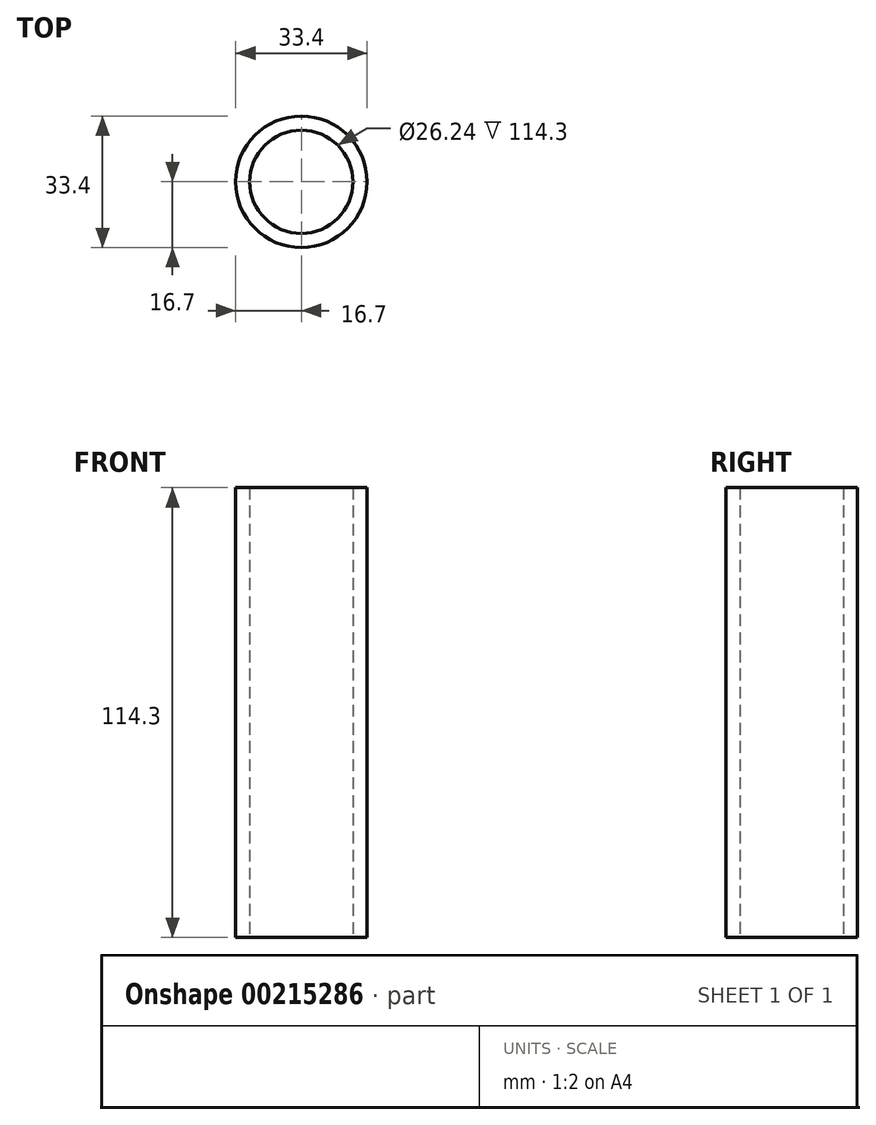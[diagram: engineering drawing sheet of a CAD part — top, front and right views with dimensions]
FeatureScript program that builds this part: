
annotation { "Feature Type Name" : "Feature", "Feature Type Description" : "" }
export const myFeature = defineFeature(function(context is Context, id is Id, definition is map)
    precondition{}
    {
        {
            var Q0;
            Q0=qCreatedBy(makeId("Top.planeOp"),FACE);
            var sketch = newSketch(context, id + "F0", { "sketchPlane" : qUnion([Q0])});
            skCircle(sketch, "E0", {"center": v(0, 0) * mm, "radius": 16.7 * mm});
            skCircle(sketch, "E1", {"center": v(0, 0) * mm, "radius": 13.12 * mm});
            skSolve(sketch);
        }
        {
            var Q0;
            Q0=makeQuery(id+"F0.imprint","IMPRINT",FACE,{"disambiguationData":[TD([[makeQuery(id+"F0.imprint","IMPRINT",EDGE,{"derivedFrom":sQuery(id+"F0.wireOp",EDGE,"E0")}),1.0]])]});
            extrude(context, id + "F1", {"entities" : qUnion([Q0]), "depth" : 114.3 * mm});
        }
    });
